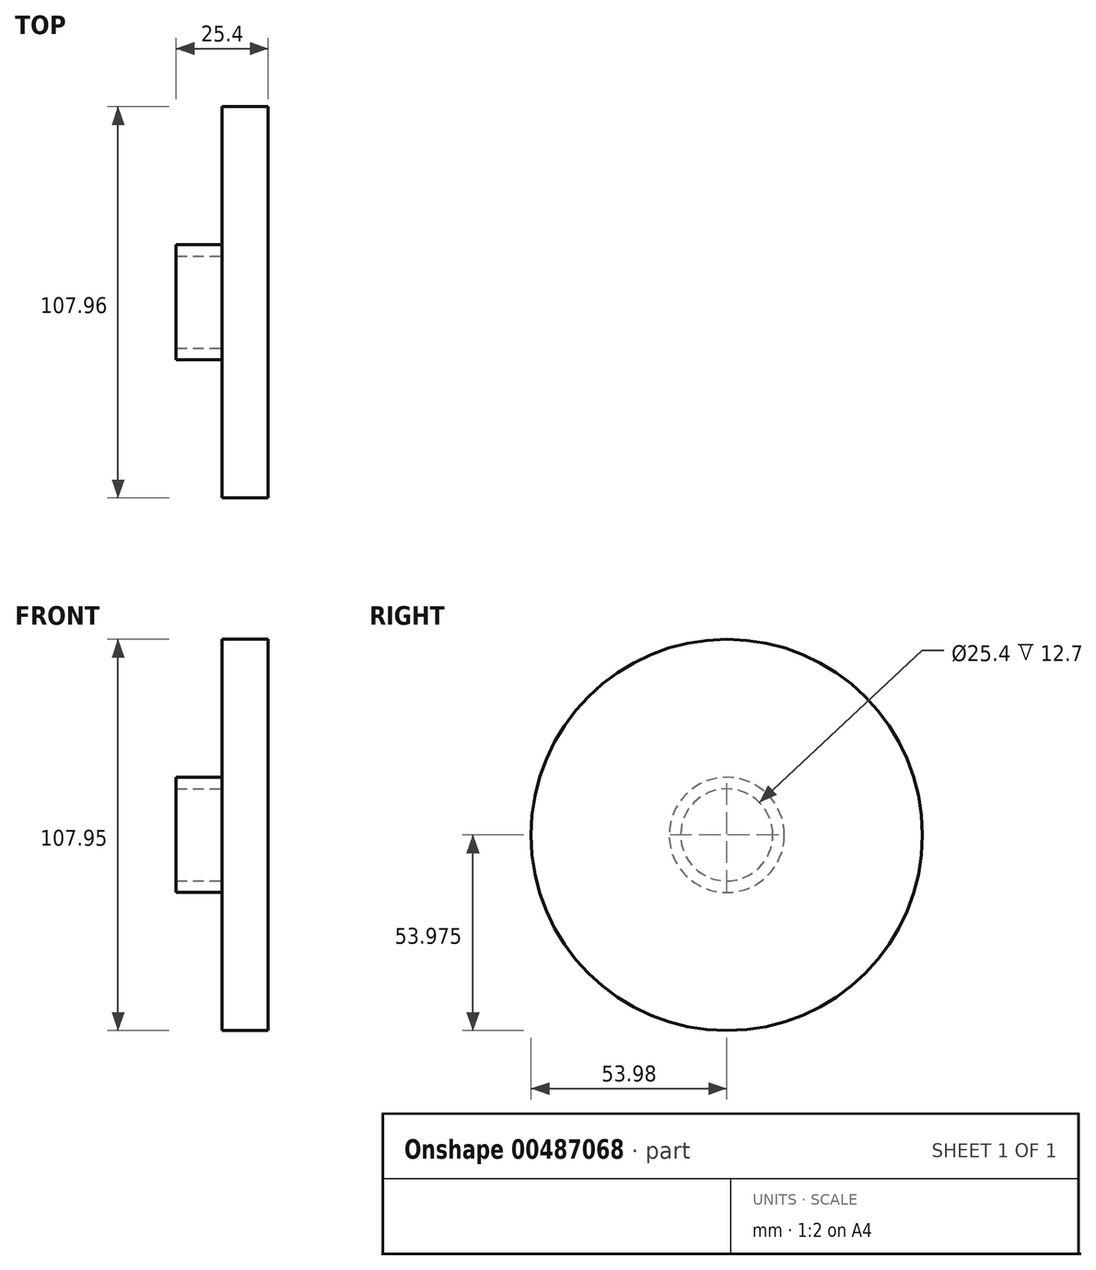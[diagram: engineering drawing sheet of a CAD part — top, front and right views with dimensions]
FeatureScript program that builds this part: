
annotation { "Feature Type Name" : "Feature", "Feature Type Description" : "" }
export const myFeature = defineFeature(function(context is Context, id is Id, definition is map)
    precondition{}
    {
        {
            var Q0;
            Q0=qCreatedBy(makeId("Front.planeOp"),FACE);
            var sketch = newSketch(context, id + "F0", { "sketchPlane" : qUnion([Q0])});
            skLineSegment(sketch, "E0", {"start": v(0, 0) * mm, "end": v(0, 9.53) * mm, "construction": true});
            skLineSegment(sketch, "E1", {"start": v(0, 9.53) * mm, "end": v(0, 63.5) * mm});
            skLineSegment(sketch, "E2", {"start": v(0, 9.53) * mm, "end": v(-25.4, 9.53) * mm});
            skLineSegment(sketch, "E3", {"start": v(-25.4, 9.53) * mm, "end": v(-25.4, 25.4) * mm});
            skLineSegment(sketch, "E4", {"start": v(0, 63.5) * mm, "end": v(-12.7, 63.5) * mm});
            skLineSegment(sketch, "E5", {"start": v(-25.4, 25.4) * mm, "end": v(-12.7, 25.4) * mm});
            skLineSegment(sketch, "E6", {"start": v(-12.7, 25.4) * mm, "end": v(-12.7, 63.5) * mm});
            skSolve(sketch);
        }
        {
            var Q0;
            Q0=makeQuery(id+"F0.imprint","IMPRINT",FACE,{"disambiguationData":[TD([[makeQuery(id+"F0.imprint","IMPRINT",EDGE,{"derivedFrom":sQuery(id+"F0.wireOp",EDGE,"E1")}),1.0]])]});
            var Q1;
            Q1=sQuery(id+"F0.wireOp",EDGE,"E2");
            revolve(context, id + "F1", {"entities" : qUnion([Q0]), "axis" : qUnion([Q1]), "revolveType" : RevolveType.FULL});
        }
        {
            var Q0;
            Q0=makeQuery(id+"F1.opRevolve","SWEPT_FACE",FACE,{"disambiguationData":[OSD([sQuery(id+"F0.wireOp",EDGE,"E6")])]});
            var sketch = newSketch(context, id + "F2", { "sketchPlane" : qUnion([Q0])});
            skCircle(sketch, "E7", {"center": v(0, 9.53) * mm, "radius": 12.7 * mm});
            skSolve(sketch);
        }
        {
            var Q0;
            Q0=sQuery(id+"F2.wireOp",VERTEX,"E7.center");
            var Q1;
            Q1=makeQuery(id+"F1.opRevolve","SWEPT_BODY",BODY,{"disambiguationData":[OSD([sQuery(id+"F0.wireOp",EDGE,"E1"),sQuery(id+"F0.wireOp",EDGE,"E2"),sQuery(id+"F0.wireOp",EDGE,"E3"),sQuery(id+"F0.wireOp",EDGE,"E4"),sQuery(id+"F0.wireOp",EDGE,"E5"),sQuery(id+"F0.wireOp",EDGE,"E6")])]});
            hole(context, id + "F3", {"style" : HoleStyle.SIMPLE, "endStyle" : HoleEndStyle.THROUGH, "oppositeDirection" : true, "holeDiameter" : 25.4 * mm, "isTappedThrough" : true, "tappedDepth" : 12.7 * mm, "tapClearance" : 3, "locations" : qUnion([Q0]), "scope" : qUnion([Q1])});
        }
    });
